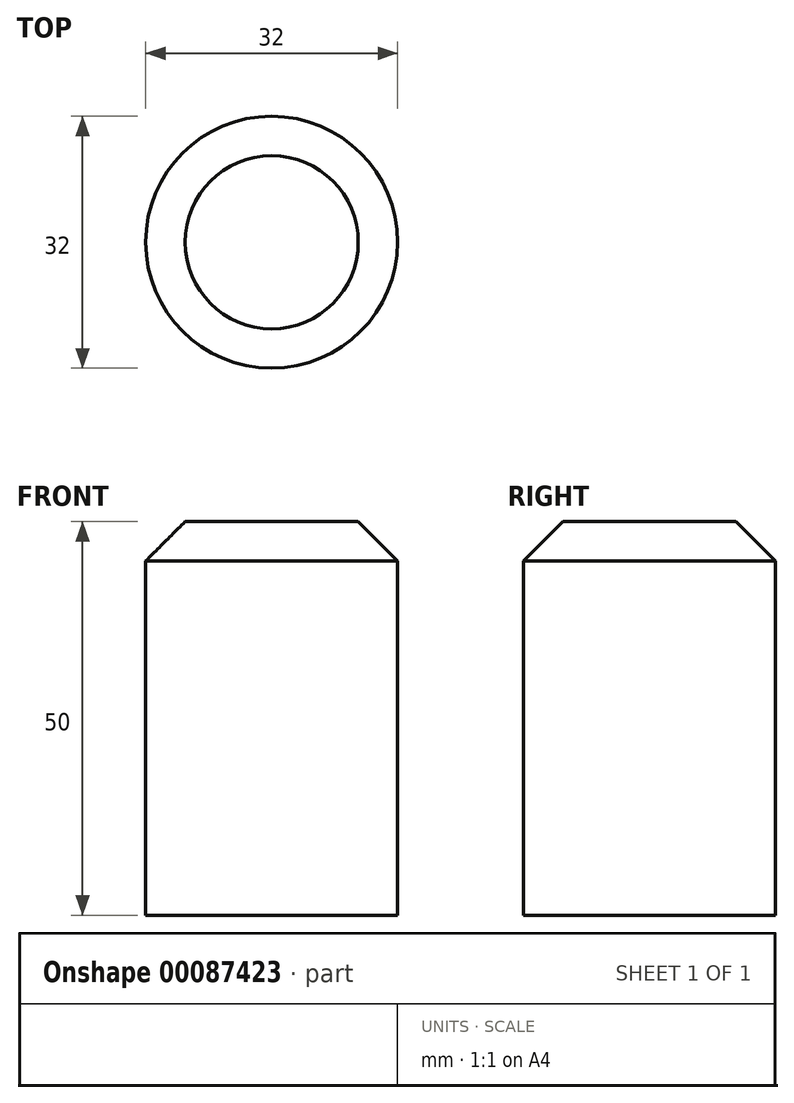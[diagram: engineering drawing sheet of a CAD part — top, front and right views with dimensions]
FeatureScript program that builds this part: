
annotation { "Feature Type Name" : "Feature", "Feature Type Description" : "" }
export const myFeature = defineFeature(function(context is Context, id is Id, definition is map)
    precondition{}
    {
        {
            var Q0;
            Q0=qCreatedBy(makeId("Front.planeOp"),FACE);
            var sketch = newSketch(context, id + "F0", { "sketchPlane" : qUnion([Q0])});
            skLineSegment(sketch, "E0.bottom", {"start": v(-16, 50) * mm, "end": v(0, 50) * mm});
            skLineSegment(sketch, "E0.top", {"start": v(-16, 0) * mm, "end": v(0, 0) * mm});
            skLineSegment(sketch, "E0.left", {"start": v(-16, 50) * mm, "end": v(-16, 0) * mm});
            skLineSegment(sketch, "E0.right", {"start": v(0, 50) * mm, "end": v(0, 0) * mm});
            skPoint(sketch, "E1", {"position": v(-69.76, 114.49) * mm});
            skPoint(sketch, "E2", {"position": v(-59.06, 98.11) * mm});
            skPoint(sketch, "E3", {"position": v(-54.33, 102.2) * mm});
            skPoint(sketch, "E4", {"position": v(0, 71.02) * mm});
            skSolve(sketch);
        }
        {
            var Q0;
            Q0=makeQuery(id+"F0.imprint","IMPRINT",FACE,{"disambiguationData":[TD([[makeQuery(id+"F0.imprint","IMPRINT",EDGE,{"derivedFrom":sQuery(id+"F0.wireOp",EDGE,"E0.bottom")}),-1.0]])]});
            var Q1;
            Q1=sQuery(id+"F0.wireOp",EDGE,"E0.right");
            revolve(context, id + "F1", {"entities" : qUnion([Q0]), "axis" : qUnion([Q1]), "revolveType" : RevolveType.FULL});
        }
        {
            var Q0;
            Q0=makeQuery(id+"F1.opRevolve","SWEPT_EDGE",EDGE,{"disambiguationData":[OSD([sQuery(id+"F0.wireOp",EDGE,"E0.bottom"),sQuery(id+"F0.wireOp",EDGE,"E0.left")])]});
            chamfer(context, id + "F2", {"entities" : qUnion([Q0]), "width" : 5 * mm, "tangentPropagation" : true});
        }
    });
